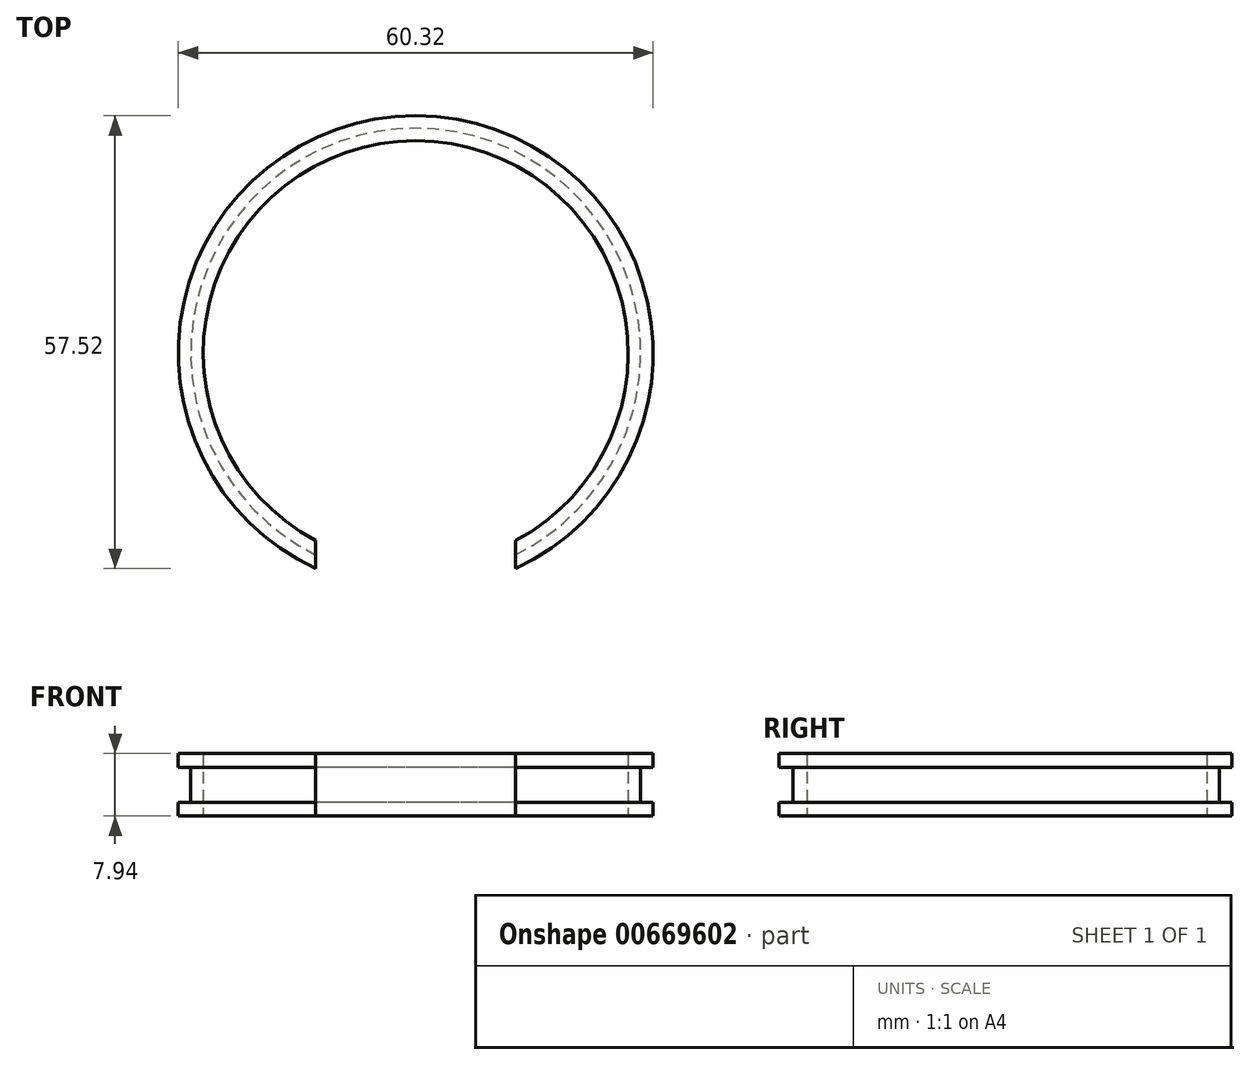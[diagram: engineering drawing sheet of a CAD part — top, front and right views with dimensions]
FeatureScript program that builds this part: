
annotation { "Feature Type Name" : "Feature", "Feature Type Description" : "" }
export const myFeature = defineFeature(function(context is Context, id is Id, definition is map)
    precondition{}
    {
        {
            var Q0;
            Q0=qCreatedBy(makeId("Top.planeOp"),FACE);
            var sketch = newSketch(context, id + "F0", { "sketchPlane" : qUnion([Q0])});
            skCircle(sketch, "E0", {"center": v(0, 0) * mm, "radius": 30.16 * mm});
            skCircle(sketch, "E1", {"center": v(0, 0) * mm, "radius": 2.87 * mm});
            skCircle(sketch, "E2", {"center": v(0, 0) * mm, "radius": 26.99 * mm});
            skSolve(sketch);
        }
        {
            var Q0;
            Q0=makeQuery(id+"F0.imprint","IMPRINT",FACE,{"disambiguationData":[TD([[makeQuery(id+"F0.imprint","IMPRINT",EDGE,{"derivedFrom":sQuery(id+"F0.wireOp",EDGE,"E0")}),1.0]])]});
            extrude(context, id + "F1", {"entities" : qUnion([Q0]), "endBound" : BoundingType.SYMMETRIC, "depth" : 7.94 * mm, "offsetDistance" : 25.4 * mm});
        }
        {
            var Q0;
            Q0=qCreatedBy(makeId("Top.planeOp"),FACE);
            var sketch = newSketch(context, id + "F2", { "sketchPlane" : qUnion([Q0])});
            skCircle(sketch, "E3", {"center": v(0, 0) * mm, "radius": 28.57 * mm});
            skCircle(sketch, "E4", {"center": v(0, 0) * mm, "radius": 36.33 * mm});
            skSolve(sketch);
        }
        {
            var Q0;
            Q0 = qSketchRegion(id + "F2", true);
            extrude(context, id + "F3", {"entities" : qUnion([Q0]), "operationType" : NewBodyOperationType.REMOVE, "endBound" : BoundingType.SYMMETRIC, "oppositeDirection" : true, "depth" : 4.44 * mm, "offsetDistance" : 25.4 * mm});
        }
        {
            var Q0;
            Q0=qCreatedBy(makeId("Top.planeOp"),FACE);
            var sketch = newSketch(context, id + "F4", { "sketchPlane" : qUnion([Q0])});
            skLineSegment(sketch, "E5.bottom", {"start": v(-12.7, 0) * mm, "end": v(12.7, 0) * mm});
            skLineSegment(sketch, "E5.top", {"start": v(-12.7, -40.86) * mm, "end": v(12.7, -40.86) * mm});
            skLineSegment(sketch, "E5.left", {"start": v(-12.7, 0) * mm, "end": v(-12.7, -40.86) * mm});
            skLineSegment(sketch, "E5.right", {"start": v(12.7, 0) * mm, "end": v(12.7, -40.86) * mm});
            skSolve(sketch);
        }
        {
            var Q0;
            Q0 = qSketchRegion(id + "F4", true);
            extrude(context, id + "F5", {"entities" : qUnion([Q0]), "operationType" : NewBodyOperationType.REMOVE, "endBound" : BoundingType.SYMMETRIC, "oppositeDirection" : true, "depth" : 25.4 * mm, "offsetDistance" : 25.4 * mm});
        }
    });
